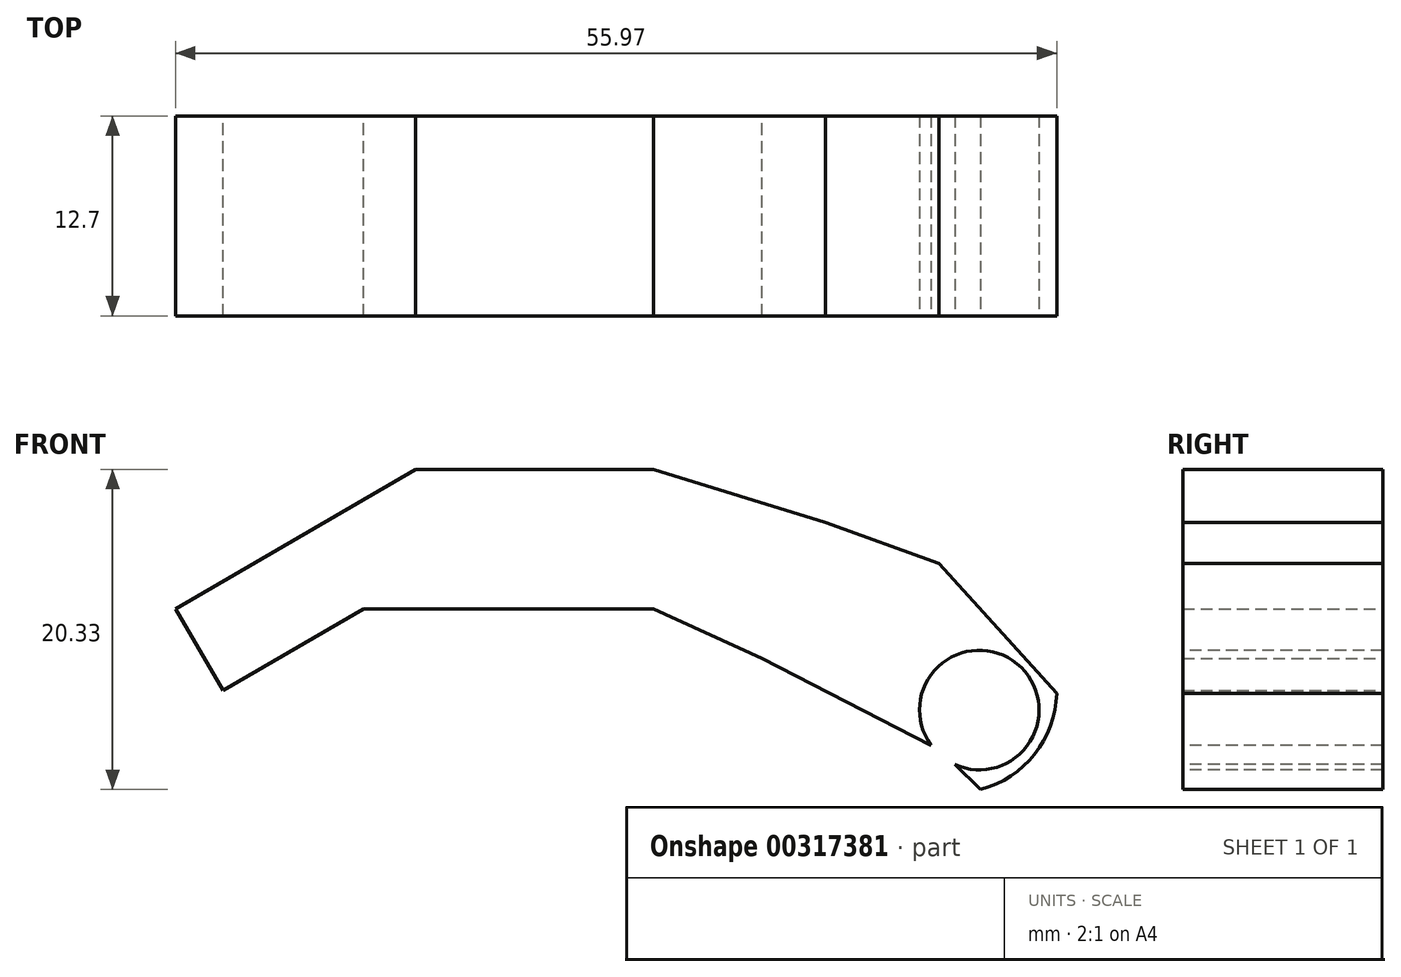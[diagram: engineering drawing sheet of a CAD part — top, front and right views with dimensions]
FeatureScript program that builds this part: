
annotation { "Feature Type Name" : "Feature", "Feature Type Description" : "" }
export const myFeature = defineFeature(function(context is Context, id is Id, definition is map)
    precondition{}
    {
        {
            var Q0;
            Q0=qCreatedBy(makeId("Front.planeOp"),FACE);
            var sketch = newSketch(context, id + "F0", { "sketchPlane" : qUnion([Q0])});
            skLineSegment(sketch, "E0", {"start": v(0, 0) * mm, "end": v(-18.42, 0) * mm});
            skLineSegment(sketch, "E1", {"start": v(-18.42, 0) * mm, "end": v(-27.34, -5.18) * mm});
            skLineSegment(sketch, "E2", {"start": v(-27.34, -5.18) * mm, "end": v(-30.35, 0) * mm});
            skLineSegment(sketch, "E3", {"start": v(-30.35, 0) * mm, "end": v(-15.12, 8.85) * mm});
            skLineSegment(sketch, "E4", {"start": v(-15.12, 8.85) * mm, "end": v(0, 8.85) * mm});
            skLineSegment(sketch, "E5", {"start": v(0, 8.85) * mm, "end": v(10.94, 5.47) * mm});
            skLineSegment(sketch, "E6", {"start": v(10.94, 5.47) * mm, "end": v(18.13, 2.88) * mm});
            skLineSegment(sketch, "E7", {"start": v(18.13, 2.88) * mm, "end": v(29.36, -9.5) * mm});
            skLineSegment(sketch, "E8", {"start": v(29.36, -9.5) * mm, "end": v(26.77, -17.27) * mm});
            skLineSegment(sketch, "E9", {"start": v(26.77, -17.27) * mm, "end": v(18.13, -8.92) * mm});
            skLineSegment(sketch, "E10", {"start": v(18.13, -8.92) * mm, "end": v(6.9, -3.17) * mm});
            skLineSegment(sketch, "E11", {"start": v(6.9, -3.17) * mm, "end": v(0, 0) * mm});
            skSolve(sketch);
        }
        {
            var Q0;
            Q0=makeQuery(id+"F0.imprint","IMPRINT",FACE,{"disambiguationData":[TD([[makeQuery(id+"F0.imprint","IMPRINT",EDGE,{"derivedFrom":sQuery(id+"F0.wireOp",EDGE,"E0")}),-1.0]])]});
            extrude(context, id + "F1", {"entities" : qUnion([Q0]), "depth" : 12.7 * mm});
        }
        {
            var Q0;
            Q0=makeQuery(id+"F1.opExtrude","CAP_FACE",FACE,{"disambiguationData":[OSD([sQuery(id+"F0.wireOp",EDGE,"E0"),sQuery(id+"F0.wireOp",EDGE,"E1"),sQuery(id+"F0.wireOp",EDGE,"E2"),sQuery(id+"F0.wireOp",EDGE,"E3"),sQuery(id+"F0.wireOp",EDGE,"E4"),sQuery(id+"F0.wireOp",EDGE,"E5"),sQuery(id+"F0.wireOp",EDGE,"E6"),sQuery(id+"F0.wireOp",EDGE,"E7"),sQuery(id+"F0.wireOp",EDGE,"E8"),sQuery(id+"F0.wireOp",EDGE,"E9"),sQuery(id+"F0.wireOp",EDGE,"E10"),sQuery(id+"F0.wireOp",EDGE,"E11")])],"isStart":false});
            var sketch = newSketch(context, id + "F2", { "sketchPlane" : qUnion([Q0])});
            skLineSegment(sketch, "E12", {"start": v(0, 0) * mm, "end": v(20.7, -6.43) * mm});
            skSolve(sketch);
        }
        {
            var Q0;
            Q0=sQuery(id+"F2.wireOp",VERTEX,"E12.end");
            var Q1;
            Q1=makeQuery(id+"F1.opExtrude","SWEPT_BODY",BODY,{"disambiguationData":[OSD([sQuery(id+"F0.wireOp",EDGE,"E0"),sQuery(id+"F0.wireOp",EDGE,"E1"),sQuery(id+"F0.wireOp",EDGE,"E2"),sQuery(id+"F0.wireOp",EDGE,"E3"),sQuery(id+"F0.wireOp",EDGE,"E4"),sQuery(id+"F0.wireOp",EDGE,"E5"),sQuery(id+"F0.wireOp",EDGE,"E6"),sQuery(id+"F0.wireOp",EDGE,"E7"),sQuery(id+"F0.wireOp",EDGE,"E8"),sQuery(id+"F0.wireOp",EDGE,"E9"),sQuery(id+"F0.wireOp",EDGE,"E10"),sQuery(id+"F0.wireOp",EDGE,"E11")])]});
            hole(context, id + "F3", {"style" : HoleStyle.SIMPLE, "endStyle" : HoleEndStyle.THROUGH, "holeDiameter" : 7.6 * mm, "tappedDepth" : 12.7 * mm, "tapClearance" : 3, "locations" : qUnion([Q0]), "scope" : qUnion([Q1])});
        }
        {
            var Q0;
            Q0=makeQuery(id+"F1.opExtrude","CAP_FACE",FACE,{"disambiguationData":[OSD([sQuery(id+"F0.wireOp",EDGE,"E0"),sQuery(id+"F0.wireOp",EDGE,"E1"),sQuery(id+"F0.wireOp",EDGE,"E2"),sQuery(id+"F0.wireOp",EDGE,"E3"),sQuery(id+"F0.wireOp",EDGE,"E4"),sQuery(id+"F0.wireOp",EDGE,"E5"),sQuery(id+"F0.wireOp",EDGE,"E6"),sQuery(id+"F0.wireOp",EDGE,"E7"),sQuery(id+"F0.wireOp",EDGE,"E8"),sQuery(id+"F0.wireOp",EDGE,"E9"),sQuery(id+"F0.wireOp",EDGE,"E10"),sQuery(id+"F0.wireOp",EDGE,"E11")])],"isStart":false});
            var sketch = newSketch(context, id + "F4", { "sketchPlane" : qUnion([Q0])});
            skArc(sketch, "E13", {"start": v(20.78, -11.48) * mm, "mid": v(24.21, -9.24) * mm, "end": v(25.62, -5.38) * mm});
            skSolve(sketch);
        }
        {
            var Q0;
            {var subQ0=sQuery(id+"F4.wireOp",EDGE,"E13");Q0=makeQuery(id+"F4.imprint","IMPRINT",FACE,{"disambiguationData":[TD([[makeQuery(id+"F4.imprint","IMPRINT",EDGE,{"derivedFrom":subQ0}),-1.0]])]});}
            extrude(context, id + "F5", {"entities" : qUnion([Q0]), "operationType" : NewBodyOperationType.REMOVE, "oppositeDirection" : true, "depth" : 25.4 * mm});
        }
    });
